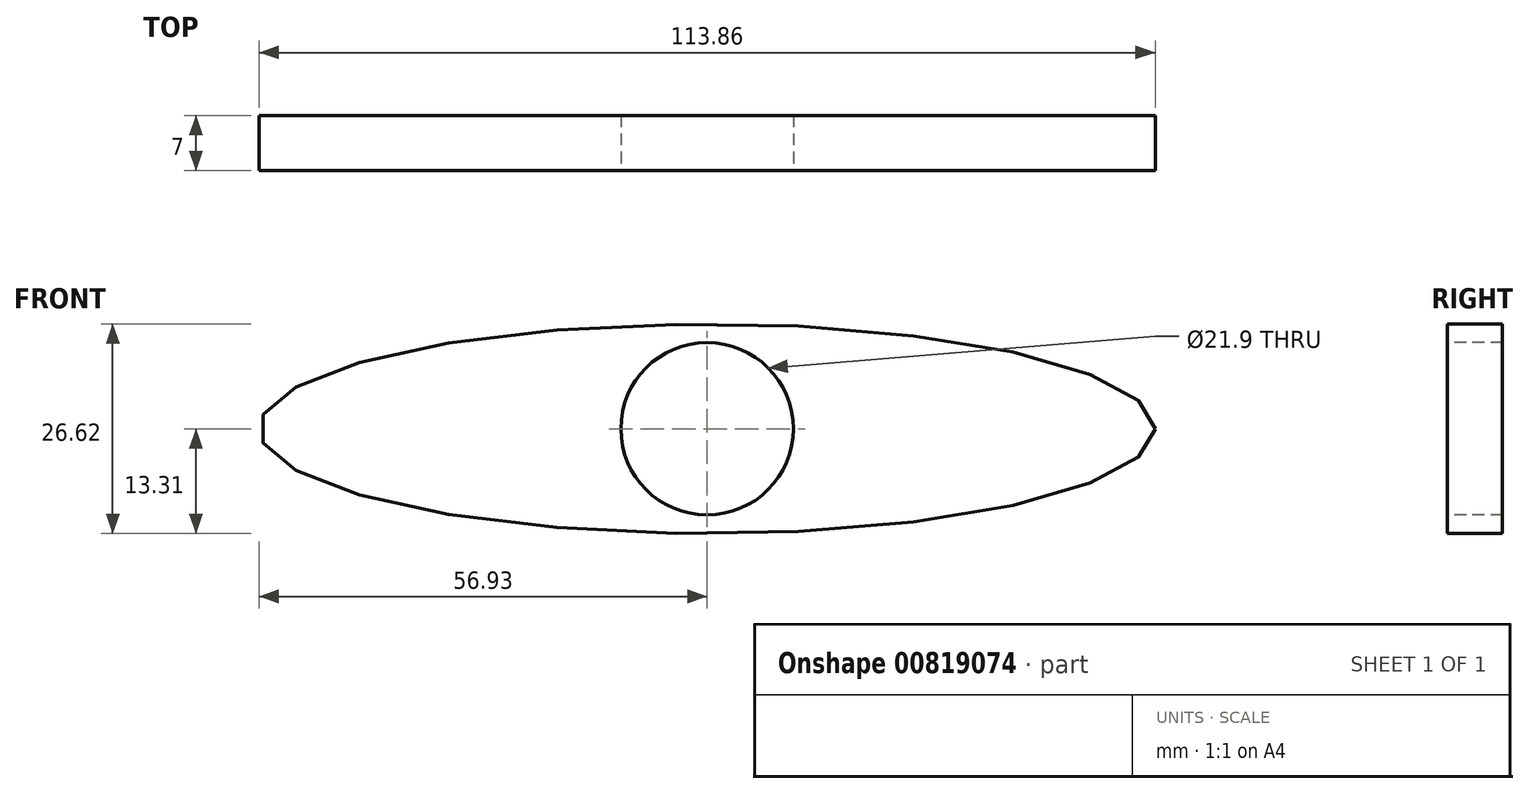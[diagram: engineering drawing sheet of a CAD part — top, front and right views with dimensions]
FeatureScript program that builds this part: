
annotation { "Feature Type Name" : "Feature", "Feature Type Description" : "" }
export const myFeature = defineFeature(function(context is Context, id is Id, definition is map)
    precondition{}
    {
        {
            var Q0;
            Q0=qCreatedBy(makeId("Front.planeOp"),FACE);
            var sketch = newSketch(context, id + "F0", { "sketchPlane" : qUnion([Q0])});
            skCircle(sketch, "E0", {"center": v(0, 0) * mm, "radius": 10.95 * mm});
            skCircle(sketch, "E1.0", {"center": v(0, 0) * mm, "radius": 12.95 * mm});
            skEllipse(sketch, "E2", {"center": v(0, 0) * mm, "majorRadius": 56.93 * mm, "minorRadius": 13.3 * mm, "majorAxis": v(1, 0)});
            skFitSpline(sketch, "E3.0", {"points": [v(58.85, -1.08) * mm, v(58.96, 0) * mm, v(58.85, 1.08) * mm, v(58.52, 2.11) * mm, v(58.01, 3.05) * mm, v(57.15, 4.2) * mm, v(55.76, 5.48) * mm, v(53.65, 6.85) * mm, v(51.1, 8.11) * mm, v(48.1, 9.28) * mm, v(45.23, 10.2) * mm, v(42.72, 10.87) * mm, v(40.72, 11.36) * mm, v(38.63, 11.83) * mm, v(35.74, 12.4) * mm, v(31.94, 13.07) * mm, v(27.1, 13.74) * mm, v(22.01, 14.3) * mm, v(16.73, 14.75) * mm, v(11.27, 15.07) * mm, v(6.62, 15.23) * mm, v(2.85, 15.3) * mm, v(0, 15.31) * mm, v(-2.85, 15.3) * mm, v(-6.62, 15.23) * mm, v(-11.27, 15.07) * mm, v(-16.73, 14.75) * mm, v(-22.01, 14.3) * mm, v(-27.1, 13.74) * mm, v(-31.94, 13.07) * mm, v(-35.74, 12.4) * mm, v(-38.63, 11.83) * mm, v(-40.72, 11.36) * mm, v(-42.72, 10.87) * mm, v(-45.23, 10.2) * mm, v(-48.1, 9.28) * mm, v(-51.1, 8.11) * mm, v(-53.65, 6.85) * mm, v(-55.76, 5.48) * mm, v(-57.15, 4.2) * mm, v(-58.01, 3.05) * mm, v(-58.52, 2.11) * mm, v(-58.85, 1.08) * mm, v(-58.96, 0) * mm, v(-58.85, -1.08) * mm, v(-58.52, -2.11) * mm, v(-58.01, -3.05) * mm, v(-57.15, -4.2) * mm, v(-55.76, -5.48) * mm, v(-53.65, -6.85) * mm, v(-51.1, -8.11) * mm, v(-48.1, -9.28) * mm, v(-45.23, -10.2) * mm, v(-42.72, -10.87) * mm, v(-40.72, -11.36) * mm, v(-38.63, -11.83) * mm, v(-35.74, -12.4) * mm, v(-31.94, -13.07) * mm, v(-27.1, -13.74) * mm, v(-22.01, -14.3) * mm, v(-16.73, -14.75) * mm, v(-11.27, -15.07) * mm, v(-6.62, -15.23) * mm, v(-2.85, -15.3) * mm, v(0, -15.31) * mm, v(2.85, -15.3) * mm, v(6.62, -15.23) * mm, v(11.27, -15.07) * mm, v(16.73, -14.75) * mm, v(22.01, -14.3) * mm, v(27.1, -13.74) * mm, v(31.94, -13.07) * mm, v(35.74, -12.4) * mm, v(38.63, -11.83) * mm, v(40.72, -11.36) * mm, v(42.72, -10.87) * mm, v(45.23, -10.2) * mm, v(48.1, -9.28) * mm, v(51.1, -8.11) * mm, v(53.65, -6.85) * mm, v(55.76, -5.48) * mm, v(57.15, -4.2) * mm, v(58.01, -3.05) * mm, v(58.52, -2.11) * mm, v(58.85, -1.08) * mm, v(58.96, 0) * mm, v(58.85, 1.08) * mm, v(58.85, -1.08) * mm]});
            skSolve(sketch);
        }
        {
            var Q0;
            Q0 = qSketchRegion(id + "F0", true);
            var Q1;
            Q1=makeQuery(id+"F0.imprint","IMPRINT",FACE,{"disambiguationData":[TD([[makeQuery(id+"F0.imprint","IMPRINT",EDGE,{"derivedFrom":sQuery(id+"F0.wireOp",EDGE,"E0")}),-1.0]])]});
            extrude(context, id + "F1", {"entities" : qUnion([Q0, Q1]), "oppositeDirection" : true, "depth" : 7 * mm, "offsetDistance" : 25 * mm});
        }
    });
